# Revit family: Haworth_Swell_PendantSixandThreeLights
name_source: partatom
category: Lighting Fixtures
revit_build: Autodesk Revit 2018 (Build: 20170223_1515(x64)
units: mm (PartAtom-declared; Revit-internal decimal feet)

## family parameters
Always vertical = Yes
Cut with Voids When Loaded = No
Light Source = Yes
OmniClass Number = 23.80.70.11.14
OmniClass Title = General Luminaries, Directional
Part Type = Normal
Room Calculation Point = No
Round Connector Dimension = Use Diameter
Shared = No
Work Plane-Based = No

## types (2) — shared parameters
Actual Height = 120"
Assembly Code = D5020200
Color Filter = 16777215
Cords Finish = Haworth _ Paint _ Metallic Silver
Dimming Lamp Color Temperature Shift = <None>
Emit Shape Visible in Rendering = No
Emit from Circle Diameter = 24"
Glass Finish = Haworth _ Glass _ Clear
Manufacturer = Haworth
Photometric Web File = generic
Revision Number = 1
Size = Verify Final Dim. w/Haworth
Tilt Angle = 60.00°
Top Finish = Haworth _ Paint _ Collection White
URL = http://www.haworth.com
URL - Product = https://www.haworth.com
Warranty = https://www.haworth.com

## per-type parameters (varying)
| type | Actual Width | Description | Six Lights | Three Lights |
| LSP3-2810 | 28" | Haworth Swell Pendants with Three Lights | No | Yes |
| LSP6-3110 | 31 1/2" | Haworth Swell Pendants with Six Lights | Yes | No |

note: column(s) folded — value = type name in every type: Model

## geometry (parser evidence)
native form markers: Sweep x6
no freeform markers — native parametric forms only
